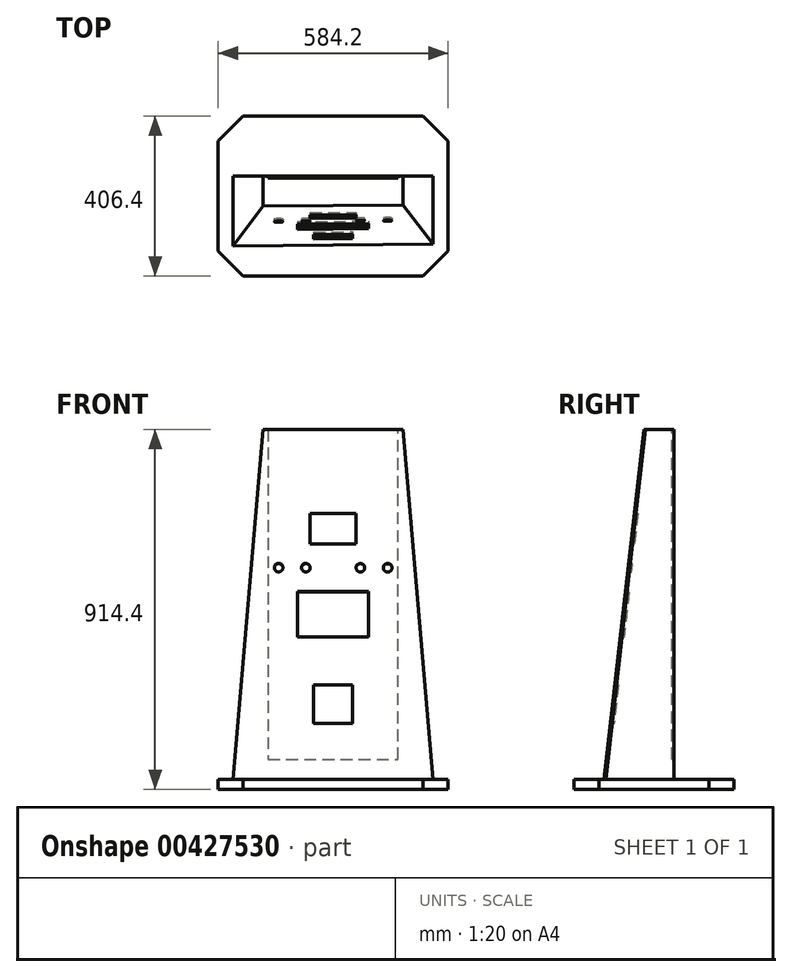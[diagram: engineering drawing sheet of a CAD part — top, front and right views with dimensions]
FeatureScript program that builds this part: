
annotation { "Feature Type Name" : "Feature", "Feature Type Description" : "" }
export const myFeature = defineFeature(function(context is Context, id is Id, definition is map)
    precondition{}
    {
        {
            var Q0;
            Q0=qCreatedBy(makeId("Front.planeOp"),FACE);
            var sketch = newSketch(context, id + "F0", { "sketchPlane" : qUnion([Q0])});
            skLineSegment(sketch, "E0", {"start": v(-254, 0) * mm, "end": v(254, 0) * mm});
            skLineSegment(sketch, "E1", {"start": v(254, 0) * mm, "end": v(177.8, 889) * mm});
            skLineSegment(sketch, "E2", {"start": v(-177.8, 889) * mm, "end": v(-254, 0) * mm});
            skLineSegment(sketch, "E3", {"start": v(0, 0) * mm, "end": v(0, 889) * mm, "construction": true});
            skLineSegment(sketch, "E4", {"start": v(177.8, 889) * mm, "end": v(0, 889) * mm});
            skLineSegment(sketch, "E5", {"start": v(0, 889) * mm, "end": v(-177.8, 889) * mm});
            skSolve(sketch);
        }
        {
            var Q0;
            {var subQ0=sQuery(id+"F0.wireOp",EDGE,"E2");Q0=makeQuery(id+"F0.imprint","IMPRINT",FACE,{"disambiguationData":[TD([[makeQuery(id+"F0.imprint","IMPRINT",EDGE,{"derivedFrom":subQ0}),1.0]])]});}
            var Q1;
            {var subQ0=sQuery(id+"F0.wireOp",EDGE,"E1");Q1=makeQuery(id+"F0.imprint","IMPRINT",FACE,{"disambiguationData":[TD([[makeQuery(id+"F0.imprint","IMPRINT",EDGE,{"derivedFrom":subQ0}),1.0]])]});}
            extrude(context, id + "F1", {"entities" : qUnion([Q0, Q1]), "oppositeDirection" : true, "depth" : 177.8 * mm});
        }
        {
            var Q0;
            Q0=makeQuery(id+"F1.opExtrude","SWEPT_FACE",FACE,{"disambiguationData":[OSD([sQuery(id+"F0.wireOp",EDGE,"E2")])]});
            var sketch = newSketch(context, id + "F2", { "sketchPlane" : qUnion([Q0])});
            skLineSegment(sketch, "E6", {"start": v(0, -21.7) * mm, "end": v(0, 1635.87) * mm});
            skLineSegment(sketch, "E7", {"start": v(0, 1635.87) * mm, "end": v(-187.84, 1635.87) * mm});
            skLineSegment(sketch, "E8", {"start": v(-187.84, 1635.87) * mm, "end": v(0, -21.7) * mm});
            skSolve(sketch);
        }
        {
            var Q0;
            {var subQ0=sQuery(id+"F2.wireOp",EDGE,"E8");var subQ1=sQuery(id+"F2.wireOp",EDGE,"E6");var subQ2=sQuery(id+"F0.wireOp",EDGE,"E2");var subQ3=makeQuery(id+"F2.imprint","INTERSECT",VERTEX,{"derivedFrom":[makeQuery(id+"F1.opExtrude","SWEPT_EDGE",EDGE,{"disambiguationData":[OSD([sQuery(id+"F0.wireOp",EDGE,"E0"),subQ2])]}),subQ1,subQ0]});Q0=makeQuery(id+"F2.imprint","IMPRINT",FACE,{"disambiguationData":[TD([[makeQuery(id+"F2.imprint","IMPRINT",EDGE,{"disambiguationData":[TD([[subQ3,1.0]])],"derivedFrom":subQ1}),-1.0]])]});}
            var Q1;
            {var subQ3=sQuery(id+"F2.wireOp",EDGE,"E7");Q1=makeQuery(id+"F2.imprint","IMPRINT",FACE,{"disambiguationData":[TD([[makeQuery(id+"F2.imprint","IMPRINT",EDGE,{"derivedFrom":subQ3}),1.0]])]});}
            extrude(context, id + "F3", {"entities" : qUnion([Q0, Q1]), "operationType" : NewBodyOperationType.REMOVE, "endBound" : BoundingType.THROUGH_ALL, "oppositeDirection" : true, "depth" : 25.4 * mm});
        }
        {
            var Q0;
            Q0=makeQuery(id+"F1.opExtrude","CAP_FACE",FACE,{"disambiguationData":[OSD([sQuery(id+"F0.wireOp",EDGE,"E0"),sQuery(id+"F0.wireOp",EDGE,"E1"),sQuery(id+"F0.wireOp",EDGE,"E2"),sQuery(id+"F0.wireOp",EDGE,"E4"),sQuery(id+"F0.wireOp",EDGE,"E5")])],"isStart":false});
            var sketch = newSketch(context, id + "F4", { "sketchPlane" : qUnion([Q0])});
            skLineSegment(sketch, "E9", {"start": v(-254, 0) * mm, "end": v(254, 0) * mm});
            skLineSegment(sketch, "E10", {"start": v(254, 0) * mm, "end": v(292.1, 0) * mm});
            skLineSegment(sketch, "E11", {"start": v(292.1, 0) * mm, "end": v(292.1, -25.4) * mm});
            skLineSegment(sketch, "E12", {"start": v(292.1, -25.4) * mm, "end": v(-292.1, -25.4) * mm});
            skLineSegment(sketch, "E13", {"start": v(-292.1, -25.4) * mm, "end": v(-292.1, 0) * mm});
            skLineSegment(sketch, "E14", {"start": v(-292.1, 0) * mm, "end": v(-254, 0) * mm});
            skSolve(sketch);
        }
        {
            var Q0;
            Q0=makeQuery(id+"F4.imprint","IMPRINT",FACE,{"disambiguationData":[TD([[makeQuery(id+"F4.imprint","IMPRINT",EDGE,{"derivedFrom":sQuery(id+"F4.wireOp",EDGE,"E9")}),1.0]])]});
            extrude(context, id + "F5", {"entities" : qUnion([Q0]), "depth" : 152.4 * mm, "hasSecondDirection" : true, "secondDirectionOppositeDirection" : true, "secondDirectionDepth" : 254 * mm});
        }
        {
            var Q0;
            Q0=makeQuery(id+"F1.opExtrude","CAP_FACE",FACE,{"disambiguationData":[OSD([sQuery(id+"F0.wireOp",EDGE,"E0"),sQuery(id+"F0.wireOp",EDGE,"E1"),sQuery(id+"F0.wireOp",EDGE,"E2"),sQuery(id+"F0.wireOp",EDGE,"E4"),sQuery(id+"F0.wireOp",EDGE,"E5")])],"isStart":false});
            var sketch = newSketch(context, id + "F6", { "sketchPlane" : qUnion([Q0])});
            skLineSegment(sketch, "E15", {"start": v(-165.1, 889) * mm, "end": v(165.1, 889) * mm});
            skLineSegment(sketch, "E16", {"start": v(165.1, 889) * mm, "end": v(165.1, 50.8) * mm});
            skLineSegment(sketch, "E17", {"start": v(165.1, 50.8) * mm, "end": v(-165.1, 50.8) * mm});
            skLineSegment(sketch, "E18", {"start": v(-165.1, 50.8) * mm, "end": v(-165.1, 889) * mm});
            skLineSegment(sketch, "E19.bottom", {"start": v(-152.4, 889) * mm, "end": v(152.4, 889) * mm});
            skLineSegment(sketch, "E19.top", {"start": v(-152.4, 63.5) * mm, "end": v(152.4, 63.5) * mm});
            skLineSegment(sketch, "E19.left", {"start": v(-152.4, 889) * mm, "end": v(-152.4, 63.5) * mm});
            skLineSegment(sketch, "E19.right", {"start": v(152.4, 889) * mm, "end": v(152.4, 63.5) * mm});
            skSolve(sketch);
        }
        {
            var Q0;
            Q0 = qSketchRegion(id + "F6", true);
            extrude(context, id + "F7", {"entities" : qUnion([Q0]), "operationType" : NewBodyOperationType.REMOVE, "oppositeDirection" : true, "depth" : 5.08 * mm});
        }
        {
            var Q0;
            Q0=makeQuery(id+"F5.opExtrude","SWEPT_FACE",FACE,{"disambiguationData":[OSD([sQuery(id+"F4.wireOp",EDGE,"E12")])]});
            var sketch = newSketch(context, id + "F8", { "sketchPlane" : qUnion([Q0])});
            skLineSegment(sketch, "E20", {"start": v(-228.6, 76.2) * mm, "end": v(-292.1, 12.7) * mm});
            skLineSegment(sketch, "E21", {"start": v(-292.1, 12.7) * mm, "end": v(-292.1, -266.7) * mm});
            skLineSegment(sketch, "E22", {"start": v(-292.1, -266.7) * mm, "end": v(-228.6, -330.2) * mm});
            skLineSegment(sketch, "E23", {"start": v(0, 76.2) * mm, "end": v(0, -330.2) * mm, "construction": true});
            skLineSegment(sketch, "E24", {"start": v(-292.1, -127) * mm, "end": v(292.1, -127) * mm, "construction": true});
            skPoint(sketch, "E24.endSnap0", {"position": v(-292.1, -127) * mm});
            skLineSegment(sketch, "E25", {"start": v(0, -330.2) * mm, "end": v(-228.6, -330.2) * mm});
            skLineSegment(sketch, "E26", {"start": v(0, 76.2) * mm, "end": v(-228.6, 76.2) * mm});
            skLineSegment(sketch, "E27.MirrorCS", {"start": v(228.6, 76.2) * mm, "end": v(292.1, 12.7) * mm});
            skPoint(sketch, "E28.MirrorP", {"position": v(292.1, -127) * mm});
            skLineSegment(sketch, "E29.MirrorCS", {"start": v(0, 76.2) * mm, "end": v(228.6, 76.2) * mm});
            skLineSegment(sketch, "E30.MirrorCS", {"start": v(292.1, -266.7) * mm, "end": v(228.6, -330.2) * mm});
            skLineSegment(sketch, "E31.MirrorCS", {"start": v(0, -330.2) * mm, "end": v(228.6, -330.2) * mm});
            skLineSegment(sketch, "E32.MirrorCS", {"start": v(292.1, 12.7) * mm, "end": v(292.1, -266.7) * mm});
            skSolve(sketch);
        }
        {
            var Q0;
            {var subQ0=sQuery(id+"F8.wireOp",EDGE,"E20");Q0=makeQuery(id+"F8.imprint","IMPRINT",FACE,{"disambiguationData":[TD([[makeQuery(id+"F8.imprint","IMPRINT",EDGE,{"derivedFrom":subQ0}),-1.0]])]});}
            var Q1;
            {var subQ0=sQuery(id+"F8.wireOp",EDGE,"E22");Q1=makeQuery(id+"F8.imprint","IMPRINT",FACE,{"disambiguationData":[TD([[makeQuery(id+"F8.imprint","IMPRINT",EDGE,{"derivedFrom":subQ0}),-1.0]])]});}
            var Q2;
            {var subQ0=sQuery(id+"F8.wireOp",EDGE,"E27.MirrorCS");Q2=makeQuery(id+"F8.imprint","IMPRINT",FACE,{"disambiguationData":[TD([[makeQuery(id+"F8.imprint","IMPRINT",EDGE,{"derivedFrom":subQ0}),1.0]])]});}
            var Q3;
            {var subQ0=sQuery(id+"F8.wireOp",EDGE,"E30.MirrorCS");Q3=makeQuery(id+"F8.imprint","IMPRINT",FACE,{"disambiguationData":[TD([[makeQuery(id+"F8.imprint","IMPRINT",EDGE,{"derivedFrom":subQ0}),1.0]])]});}
            extrude(context, id + "F9", {"entities" : qUnion([Q0, Q1, Q2, Q3]), "operationType" : NewBodyOperationType.REMOVE, "oppositeDirection" : true, "depth" : 25.4 * mm});
        }
        {
            var Q0;
            Q0=makeQuery(id+"F3.boolean.opBoolean","COPY",FACE,{"derivedFrom":makeQuery(id+"F3.opExtrude","SWEPT_FACE",FACE,{"disambiguationData":[OSD([sQuery(id+"F2.wireOp",EDGE,"E8")])]})});
            var sketch = newSketch(context, id + "F10", { "sketchPlane" : qUnion([Q0])});
            skLineSegment(sketch, "E33.bottom", {"start": v(-58.38, 680.8) * mm, "end": v(58.46, 680.8) * mm});
            skLineSegment(sketch, "E33.top", {"start": v(-58.38, 602.83) * mm, "end": v(58.46, 602.83) * mm});
            skLineSegment(sketch, "E33.left", {"start": v(-58.38, 680.8) * mm, "end": v(-58.38, 602.83) * mm});
            skLineSegment(sketch, "E33.right", {"start": v(58.46, 680.8) * mm, "end": v(58.46, 602.83) * mm});
            skLineSegment(sketch, "E34", {"start": v(-58.38, 680.8) * mm, "end": v(-196, 680.8) * mm, "construction": true});
            skLineSegment(sketch, "E35", {"start": v(58.46, 680.8) * mm, "end": v(196.09, 680.8) * mm, "construction": true});
            skLineSegment(sketch, "E36.bottom", {"start": v(-90.13, 480.64) * mm, "end": v(90.21, 480.64) * mm});
            skLineSegment(sketch, "E36.top", {"start": v(-90.13, 364.56) * mm, "end": v(90.21, 364.56) * mm});
            skLineSegment(sketch, "E36.left", {"start": v(-90.13, 480.64) * mm, "end": v(-90.13, 364.56) * mm});
            skLineSegment(sketch, "E36.right", {"start": v(90.21, 480.64) * mm, "end": v(90.21, 364.56) * mm});
            skLineSegment(sketch, "E37", {"start": v(-90.13, 480.64) * mm, "end": v(-213.05, 480.64) * mm, "construction": true});
            skLineSegment(sketch, "E38", {"start": v(90.21, 480.64) * mm, "end": v(213.14, 480.64) * mm, "construction": true});
            skLineSegment(sketch, "E39.bottom", {"start": v(-49.44, 242.37) * mm, "end": v(49.53, 242.37) * mm});
            skLineSegment(sketch, "E39.top", {"start": v(-49.44, 143.41) * mm, "end": v(49.53, 143.41) * mm});
            skLineSegment(sketch, "E39.left", {"start": v(-49.44, 242.37) * mm, "end": v(-49.44, 143.41) * mm});
            skLineSegment(sketch, "E39.right", {"start": v(49.53, 242.37) * mm, "end": v(49.53, 143.41) * mm});
            skLineSegment(sketch, "E40", {"start": v(-49.44, 242.37) * mm, "end": v(-233.35, 242.37) * mm, "construction": true});
            skLineSegment(sketch, "E41", {"start": v(49.53, 242.37) * mm, "end": v(233.44, 242.37) * mm, "construction": true});
            skLineSegment(sketch, "E42", {"start": v(0.04, 602.83) * mm, "end": v(0.04, 480.64) * mm, "construction": true});
            skLineSegment(sketch, "E43", {"start": v(0.04, 364.56) * mm, "end": v(0.04, 242.37) * mm, "construction": true});
            skLineSegment(sketch, "E44", {"start": v(173.09, 841.54) * mm, "end": v(182.4, 841.55) * mm, "construction": true});
            skLineSegment(sketch, "E45", {"start": v(-173.04, 841.16) * mm, "end": v(-182.35, 841.16) * mm, "construction": true});
            skCircle(sketch, "E46", {"center": v(69.34, 541.73) * mm, "radius": 11 * mm});
            skCircle(sketch, "E47", {"center": v(138.64, 541.73) * mm, "radius": 11 * mm});
            skLineSegment(sketch, "E48", {"start": v(69.34, 541.73) * mm, "end": v(0.04, 541.73) * mm, "construction": true});
            skLineSegment(sketch, "E49", {"start": v(69.34, 541.73) * mm, "end": v(138.64, 541.73) * mm, "construction": true});
            skLineSegment(sketch, "E50", {"start": v(138.64, 541.73) * mm, "end": v(207.93, 541.73) * mm, "construction": true});
            skCircle(sketch, "E51.MirrorC", {"center": v(-138.55, 541.73) * mm, "radius": 11 * mm});
            skCircle(sketch, "E52.MirrorC", {"center": v(-69.26, 541.73) * mm, "radius": 11 * mm});
            skSolve(sketch);
        }
        {
            var Q0;
            Q0 = qSketchRegion(id + "F10", true);
            extrude(context, id + "F11", {"entities" : qUnion([Q0]), "operationType" : NewBodyOperationType.REMOVE, "oppositeDirection" : true, "depth" : 6.35 * mm});
        }
    });
